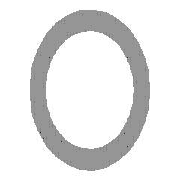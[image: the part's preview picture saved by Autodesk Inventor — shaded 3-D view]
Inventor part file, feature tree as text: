
AUTODESK INVENTOR PART (.ipt)
format: ipt  version: 2021 (Build 250183000, 183)  size: 259,072 bytes
history: native  units: mm (DEFAULTED — no unit token found)
features: other x5, plane x2, sketch x2, sweep x1
ambient origin geometry x8: Origin, YZ Plane, XZ Plane, XY Plane, X Axis, Y Axis, Z Axis, Center Point
bodies: Solid1 (feature_tree)
feature tree (10):
  parser-record x1  (decoder bookkeeping rows leaked as tree rows — omitted from the tree; the rows remain in map.json)
  other  "Driven Length"
  other  "Plano inicial"
  other  "Plano final"
  other  "Trayectoria de barrido"
  plane  "Plano de trabajo de orientación"
  sweep  "Cuerpo"
  sketch  "Sketch3"  dims[d0=33.528mm d1=4.5466mm]
  plane  "Work Plane3"
  sketch  "Sketch4"  dims[d4=-0.0mm d5=724.134184mm d6=90.0deg d7=724.134184mm d8=0.0mm d9=0.0mm]
